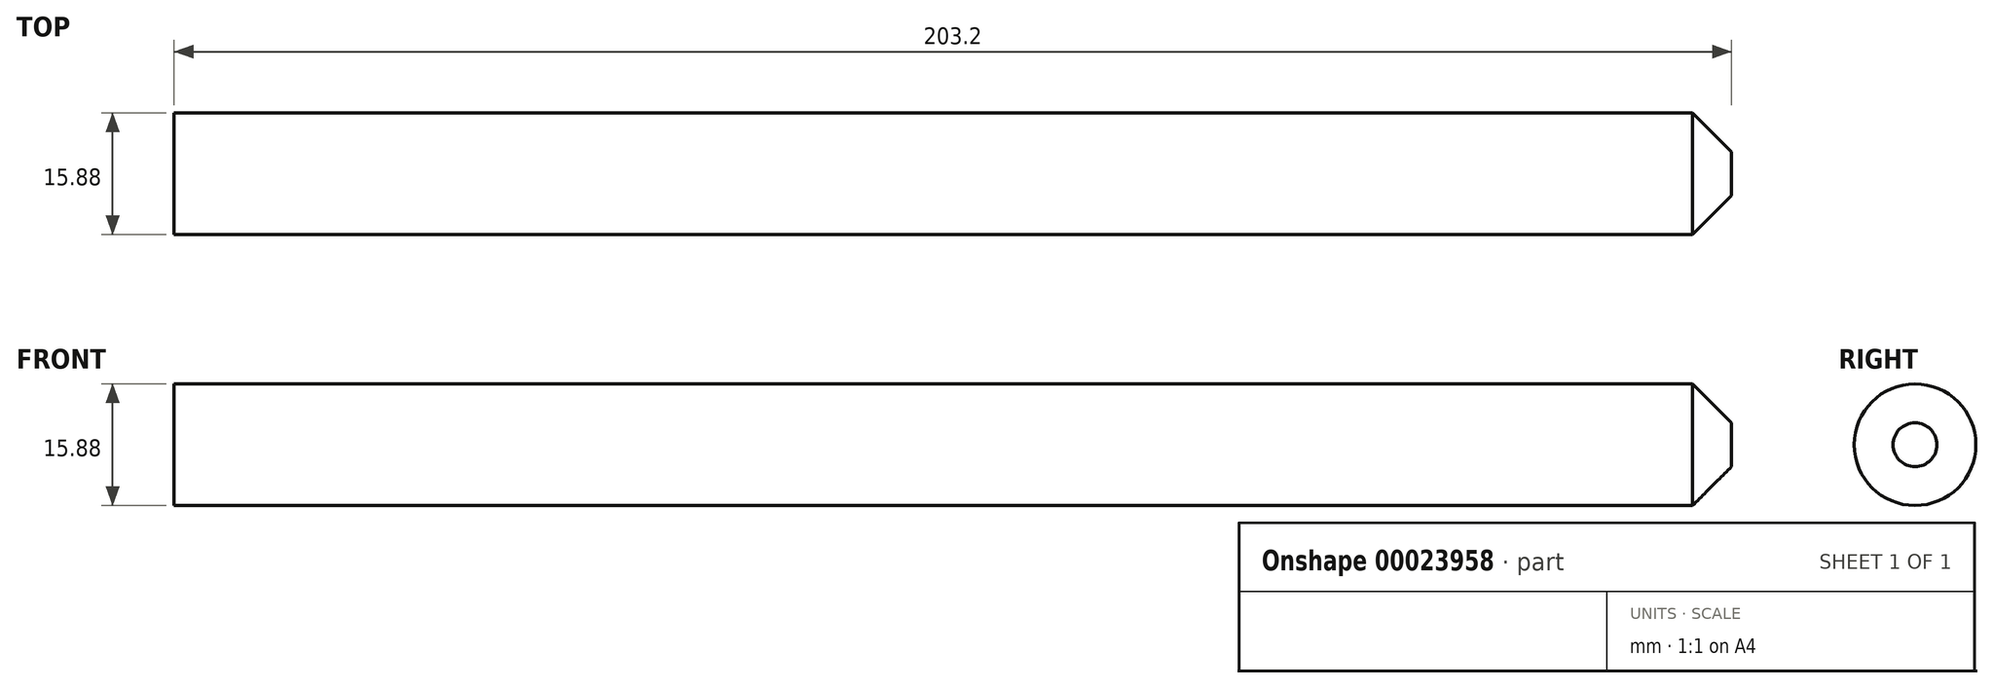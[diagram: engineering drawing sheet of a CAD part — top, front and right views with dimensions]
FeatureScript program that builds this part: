
annotation { "Feature Type Name" : "Feature", "Feature Type Description" : "" }
export const myFeature = defineFeature(function(context is Context, id is Id, definition is map)
    precondition{}
    {
        {
            var Q0;
            Q0=qCreatedBy(makeId("Right.planeOp"),FACE);
            var sketch = newSketch(context, id + "F0", { "sketchPlane" : qUnion([Q0])});
            skLineSegment(sketch, "E0.bottom", {"start": v(0, 0) * mm, "end": v(15.88, 0) * mm});
            skLineSegment(sketch, "E0.top", {"start": v(0, 15.88) * mm, "end": v(15.88, 15.88) * mm});
            skLineSegment(sketch, "E0.left", {"start": v(0, 0) * mm, "end": v(0, 15.88) * mm});
            skLineSegment(sketch, "E0.right", {"start": v(15.88, 0) * mm, "end": v(15.88, 15.88) * mm});
            skSolve(sketch);
        }
        {
            var Q0;
            Q0=makeQuery(id+"F0.imprint","IMPRINT",FACE,{"disambiguationData":[TD([[makeQuery(id+"F0.imprint","IMPRINT",EDGE,{"derivedFrom":sQuery(id+"F0.wireOp",EDGE,"E0.bottom")}),1.0]])]});
            extrude(context, id + "F1", {"entities" : qUnion([Q0]), "depth" : 203.2 * mm, "offsetDistance" : 25.4 * mm});
        }
        {
            var Q0;
            Q0=makeQuery(id+"F1.opExtrude","SWEPT_EDGE",EDGE,{"disambiguationData":[OSD([sQuery(id+"F0.wireOp",EDGE,"E0.top"),sQuery(id+"F0.wireOp",EDGE,"E0.left")])]});
            var Q1;
            Q1=makeQuery(id+"F1.opExtrude","SWEPT_EDGE",EDGE,{"disambiguationData":[OSD([sQuery(id+"F0.wireOp",EDGE,"E0.bottom"),sQuery(id+"F0.wireOp",EDGE,"E0.left")])]});
            var Q2;
            Q2=makeQuery(id+"F1.opExtrude","SWEPT_EDGE",EDGE,{"disambiguationData":[OSD([sQuery(id+"F0.wireOp",EDGE,"E0.top"),sQuery(id+"F0.wireOp",EDGE,"E0.right")])]});
            var Q3;
            Q3=makeQuery(id+"F1.opExtrude","SWEPT_EDGE",EDGE,{"disambiguationData":[OSD([sQuery(id+"F0.wireOp",EDGE,"E0.bottom"),sQuery(id+"F0.wireOp",EDGE,"E0.right")])]});
            fillet(context, id + "F2", {"entities" : qUnion([Q0, Q1, Q2, Q3]), "radius" : 7.94 * mm, "tangentPropagation" : true, "allowEdgeOverflow" : false});
        }
        {
            var Q0;
            Q0=makeQuery(id+"F1.opExtrude","CAP_FACE",FACE,{"disambiguationData":[OSD([sQuery(id+"F0.wireOp",EDGE,"E0.bottom"),sQuery(id+"F0.wireOp",EDGE,"E0.top"),sQuery(id+"F0.wireOp",EDGE,"E0.left"),sQuery(id+"F0.wireOp",EDGE,"E0.right")])],"isStart":false});
            chamfer(context, id + "F3", {"entities" : qUnion([Q0]), "width" : 5.08 * mm, "tangentPropagation" : true});
        }
        {
            var Q0;
            Q0=qCreatedBy(makeId("Front.planeOp"),FACE);
            var sketch = newSketch(context, id + "F4", { "sketchPlane" : qUnion([Q0])});
            skLineSegment(sketch, "E1", {"start": v(12.6, 15.88) * mm, "end": v(12.6, 0) * mm});
            skLineSegment(sketch, "E2", {"start": v(114.2, 0) * mm, "end": v(114.2, 15.88) * mm});
            skSolve(sketch);
        }
        {
            var Q0;
            Q0=sQuery(id+"F4.wireOp",EDGE,"E1");
            var Q1;
            Q1=sQuery(id+"F4.wireOp",EDGE,"E2");
            var Q2;
            Q2=makeQuery(id+"F2.opFillet","BLEND_FACE",FACE,{"disambiguationData":[OSD([sQuery(id+"F0.wireOp",EDGE,"E0.top"),sQuery(id+"F0.wireOp",EDGE,"E0.right")])]});
            extrude(context, id + "F5", {"bodyType" : ExtendedToolBodyType.SURFACE, "surfaceEntities" : qUnion([Q0, Q1]), "oppositeDirection" : true, "endBoundEntity" : qUnion([Q2]), "depth" : 15.88 * mm});
        }
        {
            var Q0;
            Q0=makeQuery(id+"F5.opExtrude","SWEPT_BODY",BODY,{"disambiguationData":[OSD([sQuery(id+"F4.wireOp",EDGE,"E1")])]});
            var Q1;
            Q1=makeQuery(id+"F5.opExtrude","SWEPT_BODY",BODY,{"disambiguationData":[OSD([sQuery(id+"F4.wireOp",EDGE,"E2")])]});
            deleteBodies(context, id + "F6", {"entities" : qUnion([Q0, Q1])});
        }
    });
